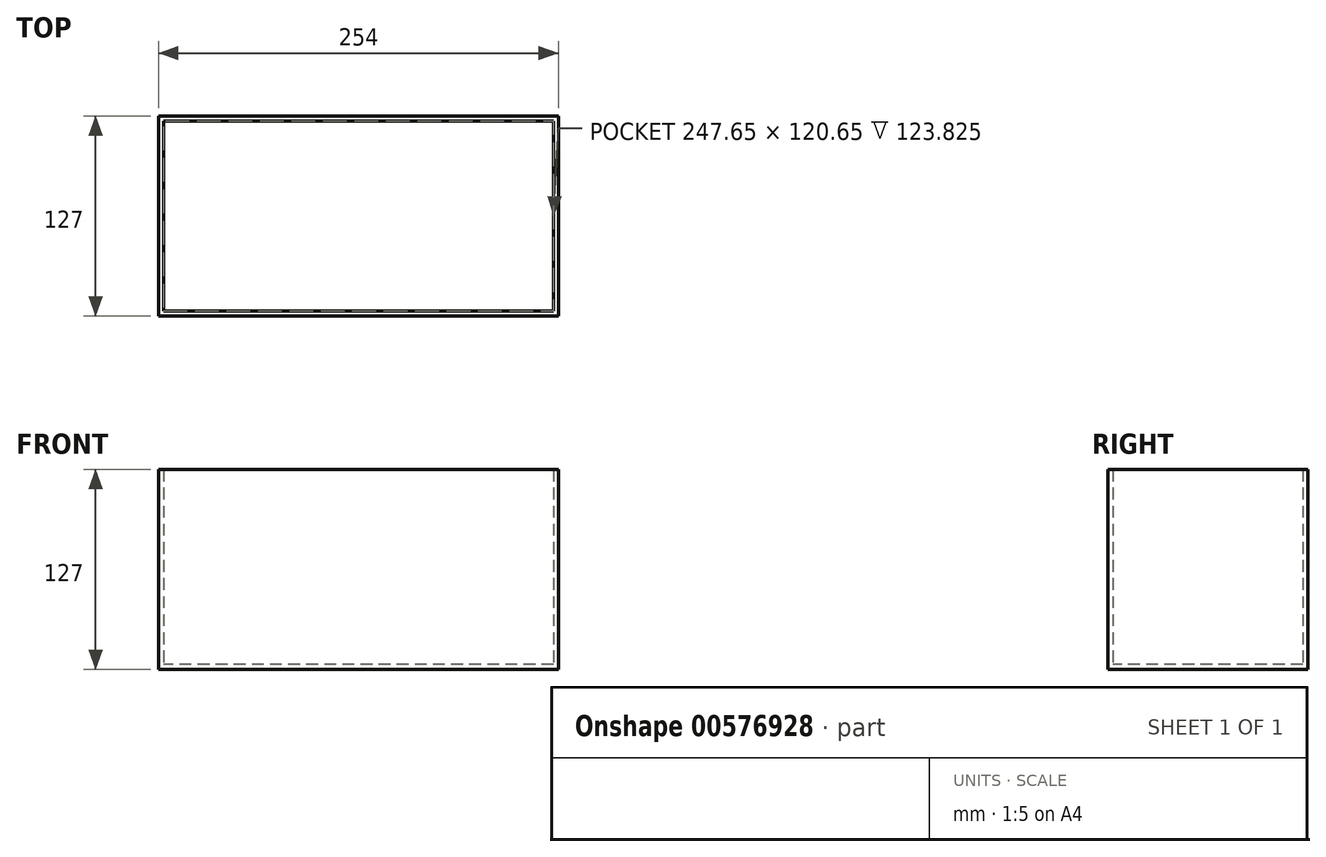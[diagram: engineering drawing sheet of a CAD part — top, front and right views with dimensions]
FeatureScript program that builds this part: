
annotation { "Feature Type Name" : "Feature", "Feature Type Description" : "" }
export const myFeature = defineFeature(function(context is Context, id is Id, definition is map)
    precondition{}
    {
        {
            var Q0;
            Q0=qCreatedBy(makeId("Top.planeOp"),FACE);
            var sketch = newSketch(context, id + "F0", { "sketchPlane" : qUnion([Q0])});
            skLineSegment(sketch, "E0.bottom", {"start": v(0, 0) * mm, "end": v(254, 0) * mm});
            skLineSegment(sketch, "E0.top", {"start": v(0, 127) * mm, "end": v(254, 127) * mm});
            skLineSegment(sketch, "E0.left", {"start": v(0, 0) * mm, "end": v(0, 127) * mm});
            skLineSegment(sketch, "E0.right", {"start": v(254, 0) * mm, "end": v(254, 127) * mm});
            skLineSegment(sketch, "E1.bottom", {"start": v(3.17, 3.18) * mm, "end": v(250.83, 3.18) * mm});
            skLineSegment(sketch, "E1.top", {"start": v(3.17, 123.83) * mm, "end": v(250.83, 123.83) * mm});
            skLineSegment(sketch, "E1.left", {"start": v(3.17, 3.17) * mm, "end": v(3.17, 123.83) * mm});
            skLineSegment(sketch, "E1.right", {"start": v(250.83, 3.17) * mm, "end": v(250.83, 123.83) * mm});
            skSolve(sketch);
        }
        {
            var Q0;
            Q0=qCreatedBy(makeId("Top.planeOp"),FACE);
            var sketch = newSketch(context, id + "F1", { "sketchPlane" : qUnion([Q0])});
            skLineSegment(sketch, "E2.bottom", {"start": v(0, 0) * mm, "end": v(254, 0) * mm});
            skLineSegment(sketch, "E2.top", {"start": v(0, 127) * mm, "end": v(254, 127) * mm});
            skLineSegment(sketch, "E2.left", {"start": v(0, 0) * mm, "end": v(0, 127) * mm});
            skLineSegment(sketch, "E2.right", {"start": v(254, 0) * mm, "end": v(254, 127) * mm});
            skSolve(sketch);
        }
        {
            var Q0;
            Q0=makeQuery(id+"F1.imprint","IMPRINT",FACE,{"disambiguationData":[TD([[makeQuery(id+"F1.imprint","IMPRINT",EDGE,{"derivedFrom":sQuery(id+"F1.wireOp",EDGE,"E2.bottom")}),1.0]])]});
            extrude(context, id + "F2", {"entities" : qUnion([Q0]), "depth" : 3.17 * mm, "offsetDistance" : 25.4 * mm});
        }
        {
            var Q0;
            Q0 = qSketchRegion(id + "F0", true);
            extrude(context, id + "F3", {"entities" : qUnion([Q0]), "operationType" : NewBodyOperationType.ADD, "depth" : 127 * mm, "offsetDistance" : 25.4 * mm});
        }
    });
